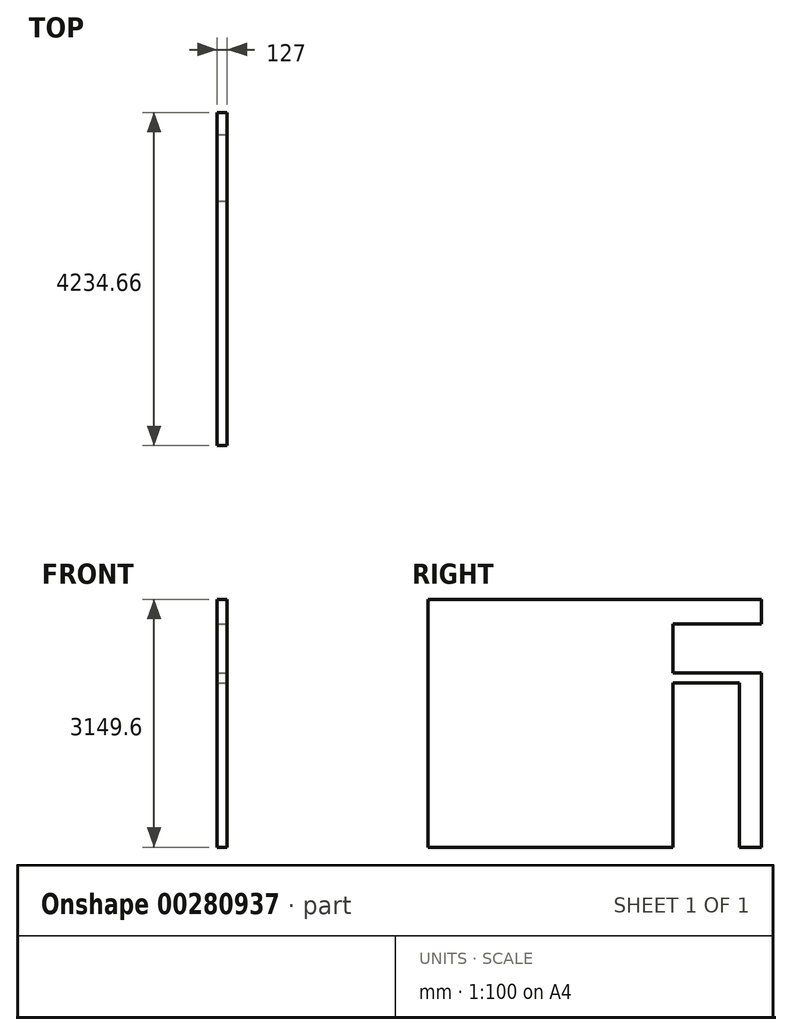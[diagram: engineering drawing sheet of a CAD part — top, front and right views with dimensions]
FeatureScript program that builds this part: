
annotation { "Feature Type Name" : "Feature", "Feature Type Description" : "" }
export const myFeature = defineFeature(function(context is Context, id is Id, definition is map)
    precondition{}
    {
        {
            var Q0;
            Q0=qCreatedBy(makeId("Top.planeOp"),FACE);
            var sketch = newSketch(context, id + "F0", { "sketchPlane" : qUnion([Q0])});
            skLineSegment(sketch, "E0.bottom", {"start": v(0, 0) * mm, "end": v(10102.06, 0) * mm});
            skLineSegment(sketch, "E0.top", {"start": v(0, 4234.66) * mm, "end": v(10102.06, 4234.66) * mm});
            skLineSegment(sketch, "E0.left", {"start": v(0, 0) * mm, "end": v(0, 4234.66) * mm});
            skLineSegment(sketch, "E0.right", {"start": v(10102.06, 0) * mm, "end": v(10102.06, 4234.66) * mm});
            skSolve(sketch);
        }
        {
            var Q0;
            Q0=makeQuery(id+"F0.imprint","IMPRINT",FACE,{"disambiguationData":[TD([[makeQuery(id+"F0.imprint","IMPRINT",EDGE,{"derivedFrom":sQuery(id+"F0.wireOp",EDGE,"E0.bottom")}),1.0]])]});
            var sketch = newSketch(context, id + "F1", { "sketchPlane" : qUnion([Q0])});
            skLineSegment(sketch, "E1.0", {"start": v(-127, 4361.66) * mm, "end": v(10229.06, 4361.66) * mm});
            skLineSegment(sketch, "E1.1", {"start": v(-127, -127) * mm, "end": v(-127, 4361.66) * mm});
            skLineSegment(sketch, "E1.2", {"start": v(-127, -127) * mm, "end": v(10229.06, -127) * mm});
            skLineSegment(sketch, "E1.3", {"start": v(10229.06, -127) * mm, "end": v(10229.06, 4361.66) * mm});
            skSolve(sketch);
        }
        {
            var Q0;
            Q0=makeQuery(id+"F1.imprint","IMPRINT",FACE,{"disambiguationData":[TD([[makeQuery(id+"F1.imprint","IMPRINT",EDGE,{"derivedFrom":sQuery(id+"F1.wireOp",EDGE,"E1.0")}),-1.0]])]});
            extrude(context, id + "F2", {"entities" : qUnion([Q0]), "depth" : 3149.6 * mm});
        }
        {
            var Q0;
            Q0=makeQuery(id+"F2.opExtrude","SWEPT_FACE",FACE,{"disambiguationData":[OSD([sQuery(id+"F0.wireOp",EDGE,"E0.left")])]});
            var sketch = newSketch(context, id + "F3", { "sketchPlane" : qUnion([Q0])});
            skLineSegment(sketch, "E2.bottom", {"start": v(4234.66, 0) * mm, "end": v(3950.5, 0) * mm, "construction": true});
            skLineSegment(sketch, "E2.top", {"start": v(4234.66, 556.25) * mm, "end": v(3950.5, 556.25) * mm, "construction": true});
            skLineSegment(sketch, "E2.left", {"start": v(4234.66, 0) * mm, "end": v(4234.66, 556.25) * mm, "construction": true});
            skLineSegment(sketch, "E2.right", {"start": v(3950.5, 0) * mm, "end": v(3950.5, 556.25) * mm, "construction": true});
            skLineSegment(sketch, "E3.bottom", {"start": v(4234.66, 0) * mm, "end": v(3110.7, 0) * mm, "construction": true});
            skLineSegment(sketch, "E3.top", {"start": v(4234.66, 556.25) * mm, "end": v(3110.7, 556.25) * mm, "construction": true});
            skLineSegment(sketch, "E3.right", {"start": v(3110.7, 0) * mm, "end": v(3110.7, 556.25) * mm, "construction": true});
            skLineSegment(sketch, "E4.bottom", {"start": v(3950.5, 0) * mm, "end": v(3110.7, 0) * mm});
            skLineSegment(sketch, "E4.top", {"start": v(3950.5, 2086.77) * mm, "end": v(3110.7, 2086.77) * mm});
            skLineSegment(sketch, "E4.left", {"start": v(3950.5, 0) * mm, "end": v(3950.5, 2086.77) * mm});
            skLineSegment(sketch, "E4.right", {"start": v(3110.7, 0) * mm, "end": v(3110.7, 2086.77) * mm});
            skSolve(sketch);
        }
        {
            var Q0;
            Q0=makeQuery(id+"F3.imprint","IMPRINT",FACE,{"disambiguationData":[TD([[makeQuery(id+"F3.imprint","IMPRINT",EDGE,{"derivedFrom":sQuery(id+"F3.wireOp",EDGE,"E4.bottom")}),1.0]])]});
            extrude(context, id + "F4", {"entities" : qUnion([Q0]), "operationType" : NewBodyOperationType.REMOVE, "endBound" : BoundingType.THROUGH_ALL, "oppositeDirection" : true, "depth" : 25.4 * mm});
        }
        {
            var Q0;
            Q0=makeQuery(id+"F2.opExtrude","SWEPT_FACE",FACE,{"disambiguationData":[OSD([sQuery(id+"F0.wireOp",EDGE,"E0.left")])]});
            var sketch = newSketch(context, id + "F5", { "sketchPlane" : qUnion([Q0])});
            skLineSegment(sketch, "E5.bottom", {"start": v(3110.7, 2086.77) * mm, "end": v(3309.59, 2086.77) * mm, "construction": true});
            skLineSegment(sketch, "E5.top", {"start": v(3110.7, 2213.77) * mm, "end": v(3309.59, 2213.77) * mm, "construction": true});
            skLineSegment(sketch, "E5.left", {"start": v(3110.7, 2086.77) * mm, "end": v(3110.7, 2213.77) * mm, "construction": true});
            skLineSegment(sketch, "E5.right", {"start": v(3309.59, 2086.77) * mm, "end": v(3309.59, 2213.77) * mm, "construction": true});
            skLineSegment(sketch, "E6.bottom", {"start": v(3110.7, 2213.77) * mm, "end": v(4279.1, 2213.77) * mm});
            skLineSegment(sketch, "E6.top", {"start": v(3110.7, 2670.97) * mm, "end": v(4279.1, 2670.97) * mm});
            skLineSegment(sketch, "E6.left", {"start": v(3110.7, 2213.77) * mm, "end": v(3110.7, 2670.97) * mm});
            skLineSegment(sketch, "E6.right", {"start": v(4279.1, 2213.77) * mm, "end": v(4279.1, 2670.97) * mm});
            skSolve(sketch);
        }
        {
            var Q0;
            {var subQ0=sQuery(id+"F5.wireOp",EDGE,"E6.left");Q0=makeQuery(id+"F5.imprint","IMPRINT",FACE,{"disambiguationData":[TD([[makeQuery(id+"F5.imprint","IMPRINT",EDGE,{"derivedFrom":subQ0}),-1.0]])]});}
            extrude(context, id + "F6", {"entities" : qUnion([Q0]), "operationType" : NewBodyOperationType.REMOVE, "endBound" : BoundingType.THROUGH_ALL, "oppositeDirection" : true, "depth" : 25.4 * mm});
        }
        {
            var Q0;
            Q0=makeQuery(id+"F2.opExtrude","SWEPT_FACE",FACE,{"disambiguationData":[OSD([sQuery(id+"F1.wireOp",EDGE,"E1.2")])]});
            extrude(context, id + "F7", {"entities" : qUnion([Q0]), "operationType" : NewBodyOperationType.REMOVE, "oppositeDirection" : true, "depth" : 127 * mm});
        }
        {
            var Q0;
            Q0=makeQuery(id+"F6.boolean.opBoolean","COPY",FACE,{"derivedFrom":makeQuery(id+"F6.opExtrude","SWEPT_FACE",FACE,{"disambiguationData":[OSD([sQuery(id+"F5.wireOp",EDGE,"E6.top")])]})});
            extrude(context, id + "F8", {"entities" : qUnion([Q0]), "operationType" : NewBodyOperationType.REMOVE, "oppositeDirection" : true, "depth" : 139.7 * mm});
        }
        {
            var Q0;
            Q0=makeQuery(id+"F8.boolean.opBoolean","COPY",FACE,{"derivedFrom":makeQuery(id+"F8.opExtrude","CAP_FACE",FACE,{"disambiguationData":[OSD([sQuery(id+"F5.wireOp",EDGE,"E6.top")])],"isStart":false})});
            extrude(context, id + "F9", {"entities" : qUnion([Q0]), "operationType" : NewBodyOperationType.REMOVE, "oppositeDirection" : true, "depth" : 25.4 * mm});
        }
        {
            var Q0;
            Q0=makeQuery(id+"F2.opExtrude","SWEPT_FACE",FACE,{"disambiguationData":[OSD([sQuery(id+"F1.wireOp",EDGE,"E1.3")])]});
            var Q1;
            Q1=makeQuery(id+"F2.opExtrude","SWEPT_FACE",FACE,{"disambiguationData":[OSD([sQuery(id+"F0.wireOp",EDGE,"E0.left")])]});
            extrude(context, id + "F10", {"entities" : qUnion([Q0]), "operationType" : NewBodyOperationType.REMOVE, "endBound" : BoundingType.UP_TO_SURFACE, "oppositeDirection" : true, "endBoundEntityFace" : qUnion([Q1]), "depth" : 25.4 * mm});
        }
        {
            var Q0;
            Q0=makeQuery(id+"F0.imprint","IMPRINT",FACE,{"disambiguationData":[TD([[makeQuery(id+"F0.imprint","IMPRINT",EDGE,{"derivedFrom":sQuery(id+"F0.wireOp",EDGE,"E0.bottom")}),1.0]])]});
            extrude(context, id + "F11", {"entities" : qUnion([Q0]), "operationType" : NewBodyOperationType.REMOVE, "oppositeDirection" : true, "depth" : 25.4 * mm});
        }
        {
            var Q0;
            Q0=makeQuery(id+"F2.opExtrude","SWEPT_FACE",FACE,{"disambiguationData":[OSD([sQuery(id+"F1.wireOp",EDGE,"E1.0")])]});
            extrude(context, id + "F12", {"entities" : qUnion([Q0]), "operationType" : NewBodyOperationType.REMOVE, "oppositeDirection" : true, "depth" : 127 * mm});
        }
    });
